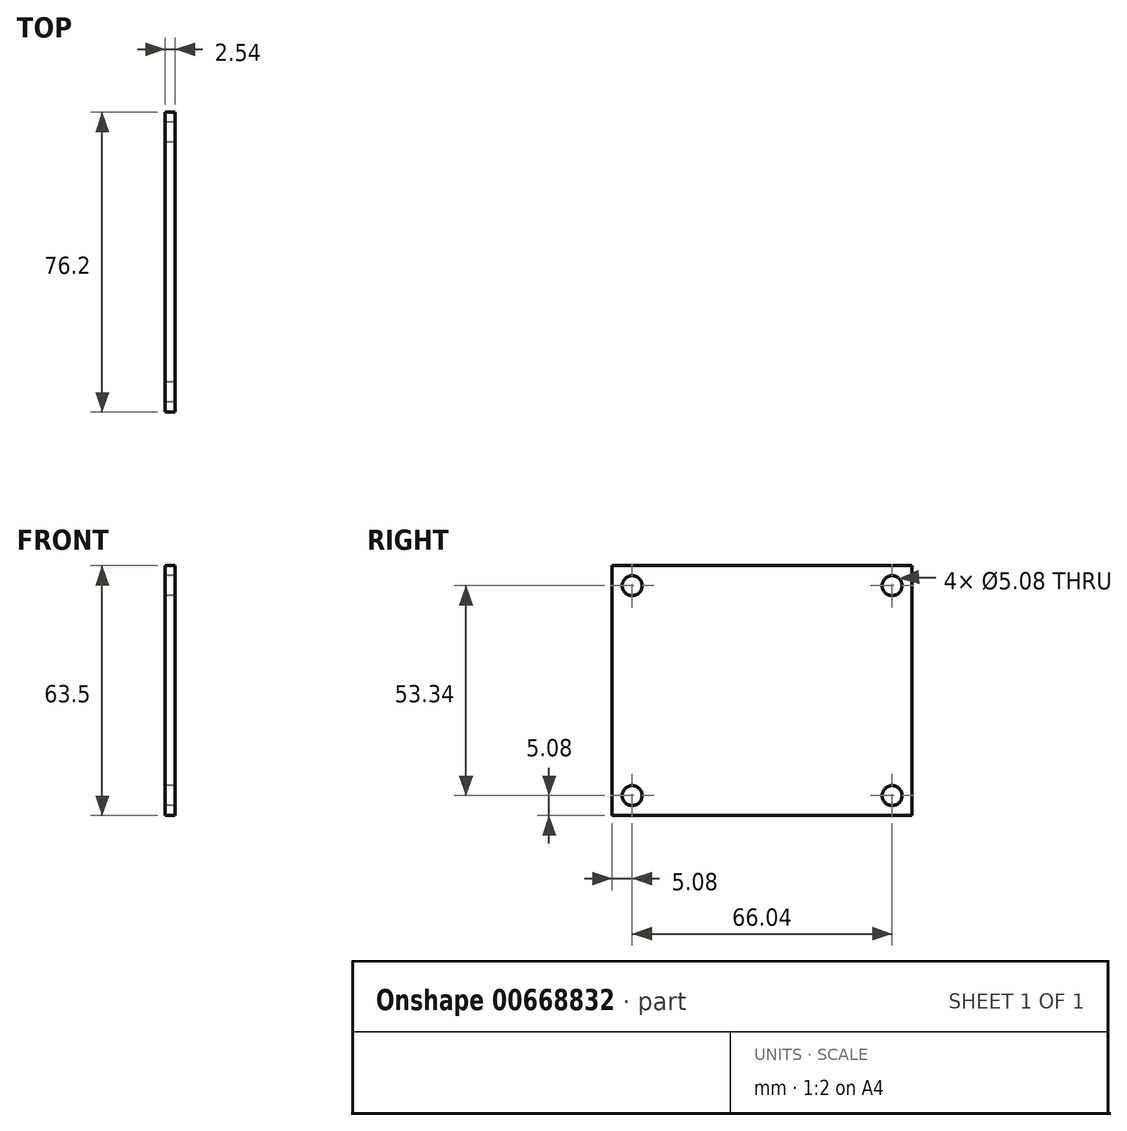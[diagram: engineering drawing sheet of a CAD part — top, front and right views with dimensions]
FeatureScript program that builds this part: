
annotation { "Feature Type Name" : "Feature", "Feature Type Description" : "" }
export const myFeature = defineFeature(function(context is Context, id is Id, definition is map)
    precondition{}
    {
        {
            var Q0;
            Q0=qCreatedBy(makeId("Right.planeOp"),FACE);
            var sketch = newSketch(context, id + "F0", { "sketchPlane" : qUnion([Q0])});
            skLineSegment(sketch, "E0.bottom", {"start": v(0, 0) * mm, "end": v(76.2, 0) * mm});
            skLineSegment(sketch, "E0.top", {"start": v(0, 63.5) * mm, "end": v(76.2, 63.5) * mm});
            skLineSegment(sketch, "E0.left", {"start": v(0, 0) * mm, "end": v(0, 63.5) * mm});
            skLineSegment(sketch, "E0.right", {"start": v(76.2, 0) * mm, "end": v(76.2, 63.5) * mm});
            skCircle(sketch, "E1", {"center": v(5.08, 58.42) * mm, "radius": 2.54 * mm});
            skCircle(sketch, "E2", {"center": v(5.08, 5.08) * mm, "radius": 2.54 * mm});
            skCircle(sketch, "E3", {"center": v(71.12, 58.42) * mm, "radius": 2.54 * mm});
            skCircle(sketch, "E4", {"center": v(71.12, 5.08) * mm, "radius": 2.54 * mm});
            skSolve(sketch);
        }
        {
            var Q0;
            Q0=makeQuery(id+"F0.imprint","IMPRINT",FACE,{"disambiguationData":[TD([[makeQuery(id+"F0.imprint","IMPRINT",EDGE,{"derivedFrom":sQuery(id+"F0.wireOp",EDGE,"E0.bottom")}),1.0]])]});
            extrude(context, id + "F1", {"entities" : qUnion([Q0]), "depth" : 2.54 * mm, "offsetDistance" : 25.4 * mm});
        }
    });
